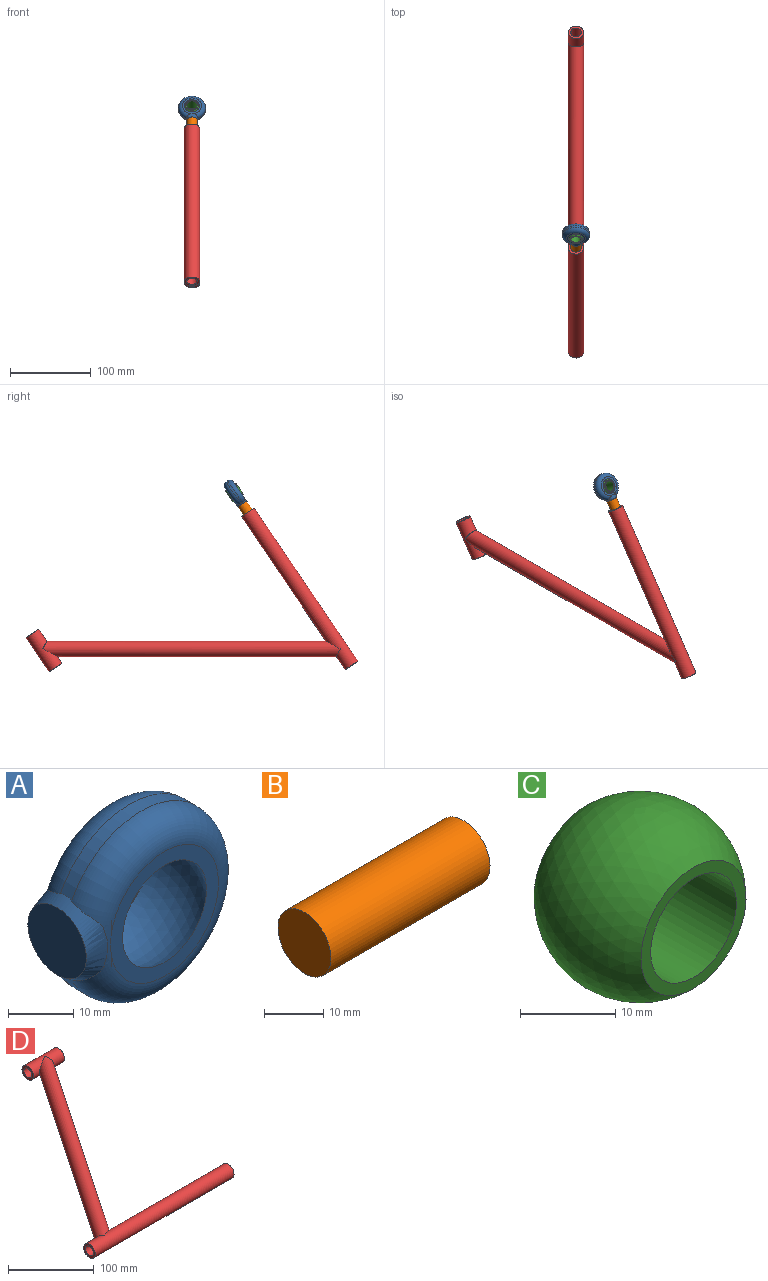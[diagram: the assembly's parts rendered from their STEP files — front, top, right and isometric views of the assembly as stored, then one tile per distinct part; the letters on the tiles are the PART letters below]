
ASSEMBLY  parts=4 mates=4
PART A: 16 faces, bbox 36.7x13.2x36.7 mm
  f0: torus R=11.75mm, axis (0,-1,0), area 658.4mm2, adj f1,f2,f3,f11,f12,f13
  f1: plane 1.95x0.31mm, normal (1,0,0), area 0mm2, adj f0,f2
  f2: bspline ~0.52x0.02mm, area 0mm2, adj f0,f1
  f3: cylinder r=16.83mm len=33.66mm, axis (0,1,0), area 228.7mm2, adj f0,f4,f13
  f4: torus R=11.75mm, axis (0,-1,0), area 670.7mm2, adj f3,f5,f7,f8,f9,f10,f13
  f5: plane 23.5x23.5mm, normal (0,-1,0), area 172.3mm2, adj f4,f6
  f6: sphere r=11.11mm, area 886.7mm2, adj f5,f12
  f7: bspline ~0.63x0.03mm, area 0mm2, adj f4,f8
  f8: plane 2.02x0.12mm, normal (-1,0,0), area 0mm2, adj f4,f7
  f9: bspline ~5.36x4.15mm, area 0mm2, adj f4,f10
  f10: plane 1.81x0.22mm, normal (1,0,0), area 0mm2, adj f4,f9
  f11: plane 2.02x0.12mm, normal (1,0,0), area 0mm2, adj f0,f13
  f12: plane 23.54x23.26mm, normal (0,1,0), area 171.3mm2, adj f0,f6,f13
  f13: bspline ~20.21x12.88mm, area 143.7mm2, adj f0,f3,f4,f11,f12,f14,f15
  f14: plane 12.86x12.86mm, normal (-1,0,0), area 126.7mm2, adj f13
  f15: torus R=11.75mm, axis (0,-1,0), area 0.5mm2, adj f13
PART B: 3 faces, bbox 38.1x12.7x12.7 mm
  f0: cylinder r=6.35mm len=38.1mm, axis (1,0,0), area 1520.1mm2, adj f1,f2
  f1: plane 12.7x12.7mm, normal (-1,0,0), area 126.7mm2, adj f0
  f2: plane 12.7x12.7mm, normal (1,0,0), area 126.7mm2, adj f0
PART C: 4 faces, bbox 22.2x15.9x22.2 mm
  f0: cylinder r=6.35mm len=15.88mm, axis (0,1,0), area 633.4mm2, adj f1,f3
  f1: plane 15.55x15.55mm, normal (0,1,0), area 63.3mm2, adj f0,f2
  f2: sphere r=11.11mm, area 1108.4mm2, adj f1,f3
  f3: plane 15.55x15.55mm, normal (0,-1,0), area 63.3mm2, adj f0,f2
PART D: 12 faces, bbox 254x323.9x19.1 mm
  f0: cylinder r=6.48mm len=50.8mm, axis (1,0,0), area 2067.4mm2, adj f7,f8
  f1: cylinder r=9.53mm len=50.8mm, axis (1,0,0), area 2602mm2, adj f2,f7,f8
  f2: cylinder r=9.53mm len=315.48mm, axis (-0.56,-0.83,0), area 21153mm2, adj f1,f6
  f3: plane 19.05x19.05mm, normal (-1,0,0), area 153.2mm2, adj f5,f6
  f4: plane 19.05x19.05mm, normal (1,0,0), area 153.2mm2, adj f5,f6
  f5: cylinder r=6.48mm len=228.6mm, axis (-1,0,0), area 9303.1mm2, adj f3,f4
  f6: cylinder r=9.53mm len=228.6mm, axis (-1,0,0), area 13242.8mm2, adj f2,f3,f4
  f7: plane 19.05x19.05mm, normal (1,0,0), area 153.2mm2, adj f0,f1
  f8: plane 19.05x19.05mm, normal (-1,0,0), area 153.2mm2, adj f0,f1
  f9: cylinder r=9.53mm len=15.65mm, axis (1,0,0), area 170.4mm2, adj f11
  f10: cylinder r=9.53mm len=15.65mm, axis (-1,0,0), area 170.5mm2, adj f11
  f11: cylinder r=6.48mm len=300.5mm, axis (-0.56,-0.83,0), area 14164mm2, adj f9,f10
PLACE A rot(axis=(0.69,0.21,0.69),156.1deg) t=(0,175.51,-267.68)mm
PLACE B rot(axis=(-0.28,-0.92,0.28),94.9deg) t=(0,-566.11,234.45)mm
PLACE C rot(axis=(0,0.29,0.96),180deg) t=(253.43,317.6,-57.83)mm
PLACE D rot(axis=(-0.28,-0.92,0.28),94.9deg) t=(0,-67.98,171.42)mm
MATE fastened A.f14 <-> B.f0  axis (0,-0.56,-0.83) through (0,-62.64,179.3)mm
MATE ball A.f0 <-> C.f0  axis (0,-0.83,0.56) through (0,-53.05,193.13)mm
MATE fastened D.f6 <-> B.f0  axis (0,0.56,0.83) through (0,-69.76,168.79)mm
MATE fastened C.f0 <-> A.f0  axis (0,-0.83,0.56) through (0,-53.05,193.13)mm
